# Revit family: E-925
name_source: partatom
category: Aparatos sanitarios
revit_build: Autodesk Revit 2016 (Build: 20150220_1215(x64)
units: mm (PartAtom-declared; Revit-internal decimal feet)

## family parameters
Compartido = Sí
Corte con vacíos al cargar = No
Cota de conector redondo = Diámetro de uso
Número OmniClass = 23.45.00.00
Punto de cálculo de habitación = No
Se basa en plano de trabajo = Sí
Siempre vertical = Sí
Tipo de pieza = Normal
Título OmniClass = Sanitary, Laundry, and Cleaning Equipment

## types (1)
- E-925
    Accesorios = Contra de Push, Inserto para Rebosadero, Herramienta para Sujeción, Llave para Aireador, Llave para Mantenimiento, Llave 5/64".
    Altura Total = 10"
    Anchura Total = 2"
    Características del Producto = Monomando alto para lavabo con desagüe de push.
    Cartucho = Cartucho Ø25 mm con vástago metálico.
    Comentarios de tipo = Monomando Alto para Lavabo con Desagüe de Push
    Cuerpo de Latón = Brass
    Descripción = Monomando alto Nautilia E-925
    Elevación por defecto = 35"
    Fabricante = HELVEX S.A. de C.V.
    Ficha Técnica = http://www.helvex.com
    Garantía = El producto HELVEX está garantizado como libre de defectos en materiales y procesos de fabricación. El producto HELVEX está garantizado, en lo que se refiere a los acabados; por un periodo de 10 años en los acabados cromo y duravex, y por 2 años en acabados diferentes al cromo, a partir de la fecha de compra indicada en la factura.
    Guía de Instalación = http://www.helvex.com
    Instalación = Conexión ½ - 14 NPSM
    Modelo = E-925
    Operación = Levante el maneral para abrir el flujo y gire a la derecha para más fría o a la izquierda para más caliente.
    Presión Máxima de Trabajo = 85.3 psi
    Presión Mínima de Trabajo = 8.5 psi
    Profundidad Total = 8"
    URL = http://www.helvex.com

## geometry (parser evidence)
native form markers: Sweep x3
no freeform markers — native parametric forms only
